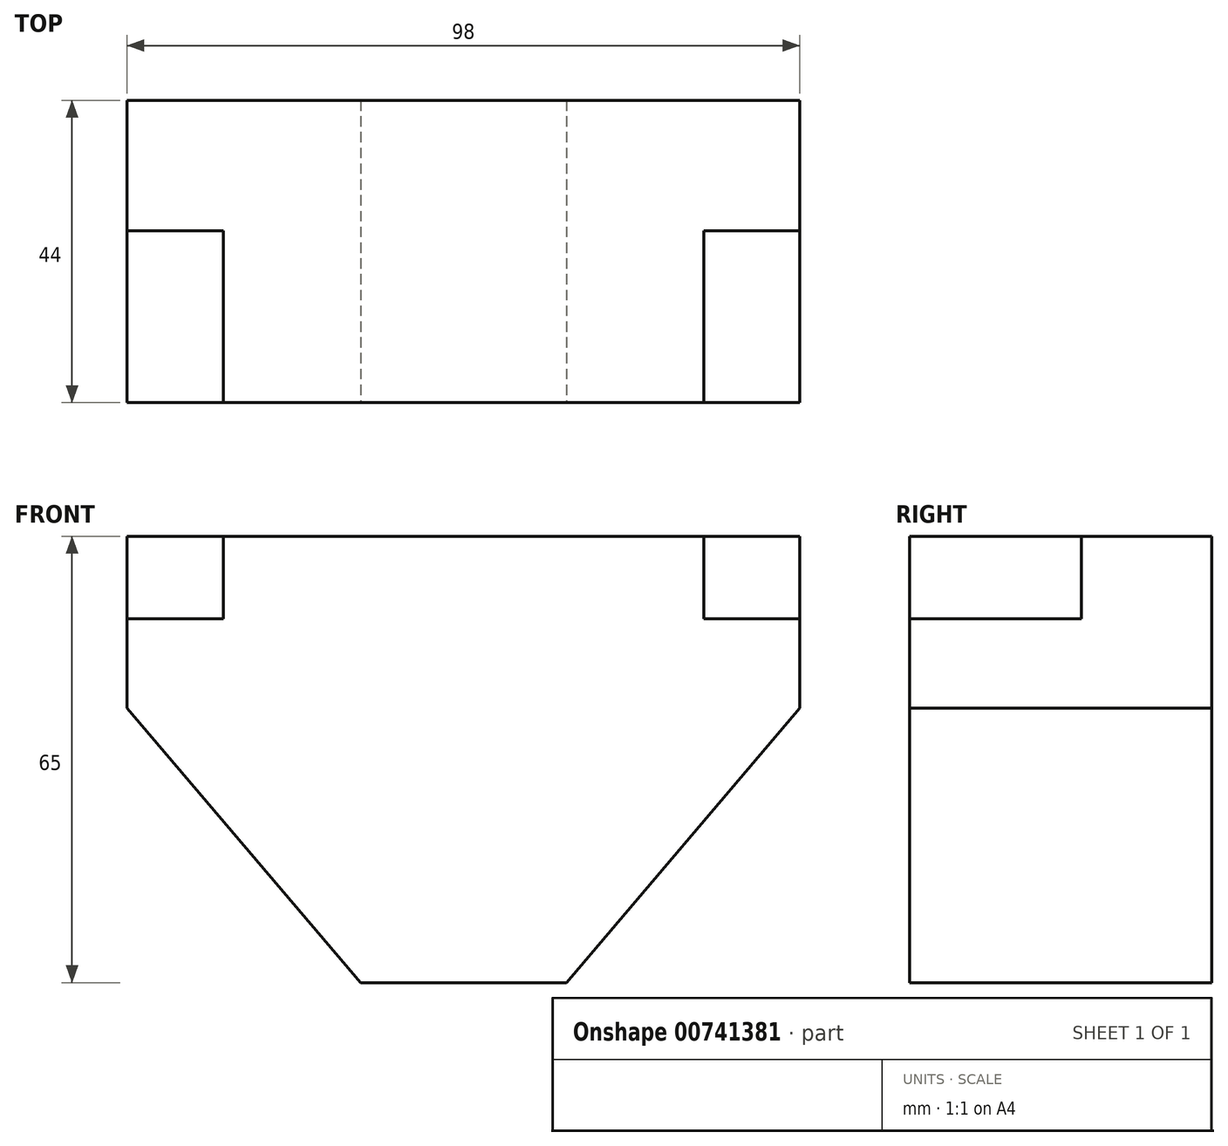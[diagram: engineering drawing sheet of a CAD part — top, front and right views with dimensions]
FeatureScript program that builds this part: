
annotation { "Feature Type Name" : "Feature", "Feature Type Description" : "" }
export const myFeature = defineFeature(function(context is Context, id is Id, definition is map)
    precondition{}
    {
        {
            var Q0;
            Q0=qCreatedBy(makeId("Front.planeOp"),FACE);
            var sketch = newSketch(context, id + "F0", { "sketchPlane" : qUnion([Q0])});
            skLineSegment(sketch, "E0.bottom", {"start": v(-49, 32.5) * mm, "end": v(49, 32.5) * mm});
            skLineSegment(sketch, "E0.top", {"start": v(-49, -32.5) * mm, "end": v(49, -32.5) * mm});
            skLineSegment(sketch, "E0.left", {"start": v(-49, 32.5) * mm, "end": v(-49, -32.5) * mm});
            skLineSegment(sketch, "E0.right", {"start": v(49, 32.5) * mm, "end": v(49, -32.5) * mm});
            skPoint(sketch, "E0.middle", {"position": v(0, 0) * mm});
            skSolve(sketch);
        }
        {
            var Q0;
            Q0 = qSketchRegion(id + "F0", true);
            extrude(context, id + "F1", {"entities" : qUnion([Q0]), "depth" : 44 * mm, "offsetDistance" : 25 * mm});
        }
        {
            var Q0;
            Q0=makeQuery(id+"F1.opExtrude","CAP_FACE",FACE,{"disambiguationData":[OSD([sQuery(id+"F0.wireOp",EDGE,"E0.bottom"),sQuery(id+"F0.wireOp",EDGE,"E0.top"),sQuery(id+"F0.wireOp",EDGE,"E0.left"),sQuery(id+"F0.wireOp",EDGE,"E0.right")])],"isStart":false});
            var sketch = newSketch(context, id + "F2", { "sketchPlane" : qUnion([Q0])});
            skPoint(sketch, "E1", {"position": v(-35, 32.5) * mm});
            skPoint(sketch, "E2", {"position": v(35, 32.5) * mm});
            skPoint(sketch, "E3", {"position": v(-49, 20.5) * mm});
            skPoint(sketch, "E4", {"position": v(49, 20.5) * mm});
            skLineSegment(sketch, "E5.bottom", {"start": v(-49, 20.5) * mm, "end": v(-35, 20.5) * mm});
            skLineSegment(sketch, "E5.top", {"start": v(-49, 32.5) * mm, "end": v(-35, 32.5) * mm});
            skLineSegment(sketch, "E5.left", {"start": v(-49, 20.5) * mm, "end": v(-49, 32.5) * mm});
            skLineSegment(sketch, "E5.right", {"start": v(-35, 20.5) * mm, "end": v(-35, 32.5) * mm});
            skLineSegment(sketch, "E6.bottom", {"start": v(35, 32.5) * mm, "end": v(49, 32.5) * mm});
            skLineSegment(sketch, "E6.top", {"start": v(35, 20.5) * mm, "end": v(49, 20.5) * mm});
            skLineSegment(sketch, "E6.left", {"start": v(35, 32.5) * mm, "end": v(35, 20.5) * mm});
            skLineSegment(sketch, "E6.right", {"start": v(49, 32.5) * mm, "end": v(49, 20.5) * mm});
            skSolve(sketch);
        }
        {
            var Q0;
            Q0 = qSketchRegion(id + "F2", true);
            extrude(context, id + "F3", {"entities" : qUnion([Q0]), "operationType" : NewBodyOperationType.REMOVE, "oppositeDirection" : true, "depth" : 25 * mm, "offsetDistance" : 25 * mm});
        }
        {
            var Q0;
            Q0=makeQuery(id+"F1.opExtrude","CAP_FACE",FACE,{"disambiguationData":[OSD([sQuery(id+"F0.wireOp",EDGE,"E0.bottom"),sQuery(id+"F0.wireOp",EDGE,"E0.top"),sQuery(id+"F0.wireOp",EDGE,"E0.left"),sQuery(id+"F0.wireOp",EDGE,"E0.right")])],"isStart":false});
            var sketch = newSketch(context, id + "F4", { "sketchPlane" : qUnion([Q0])});
            skPoint(sketch, "E7", {"position": v(-35, -32.5) * mm});
            skPoint(sketch, "E8", {"position": v(35, -32.5) * mm});
            skPoint(sketch, "E9", {"position": v(-15, -32.5) * mm});
            skPoint(sketch, "E10", {"position": v(15, -32.5) * mm});
            skPoint(sketch, "E11", {"position": v(-49, 7.5) * mm});
            skPoint(sketch, "E12", {"position": v(49, 7.5) * mm});
            skLineSegment(sketch, "E13", {"start": v(-49, 7.5) * mm, "end": v(-15, -32.5) * mm});
            skLineSegment(sketch, "E14", {"start": v(49, 7.5) * mm, "end": v(15, -32.5) * mm});
            skSolve(sketch);
        }
        {
            var Q0;
            Q0 = qSketchRegion(id + "F4", true);
            var Q1;
            {var subQ0=sQuery(id+"F4.wireOp",EDGE,"E14");Q1=makeQuery(id+"F4.imprint","IMPRINT",FACE,{"disambiguationData":[TD([[makeQuery(id+"F4.imprint","IMPRINT",EDGE,{"derivedFrom":subQ0}),1.0]])]});}
            var Q2;
            {var subQ0=sQuery(id+"F4.wireOp",EDGE,"E13");Q2=makeQuery(id+"F4.imprint","IMPRINT",FACE,{"disambiguationData":[TD([[makeQuery(id+"F4.imprint","IMPRINT",EDGE,{"derivedFrom":subQ0}),-1.0]])]});}
            extrude(context, id + "F5", {"entities" : qUnion([Q0, Q1, Q2]), "operationType" : NewBodyOperationType.REMOVE, "endBound" : BoundingType.THROUGH_ALL, "oppositeDirection" : true, "depth" : 25 * mm, "offsetDistance" : 25 * mm});
        }
    });
